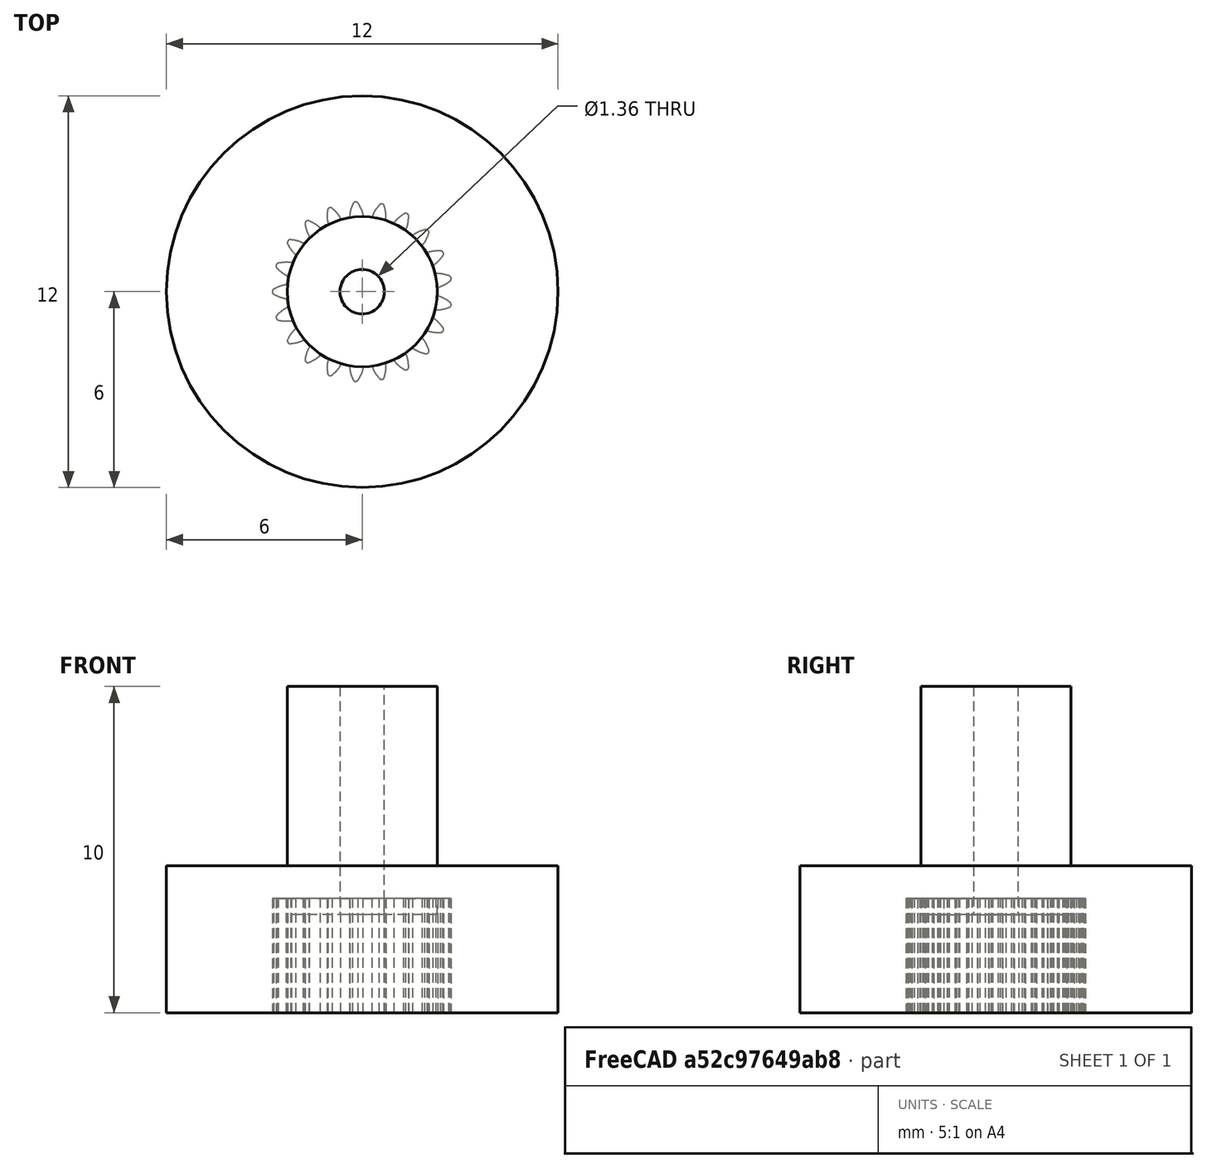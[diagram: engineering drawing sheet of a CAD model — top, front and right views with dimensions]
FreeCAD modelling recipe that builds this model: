
FCSTD DOCUMENT  (FreeCAD 0.20R29177 (Git))
Label: LC Servo top 21x024intgear short5mm
License: All rights reserved
LicenseURL: http://en.wikipedia.org/wiki/All_rights_reserved
objects: PartDesign::Body×2, PartDesign::AdditiveCylinder×2, Part::Part2DObjectPython×1, PartDesign::Pad×1, PartDesign::Boolean×1, PartDesign::SubtractiveCylinder×1, TechDraw::DrawSVGTemplate×1, PartDesign::SubtractiveBox×1, TechDraw::DrawViewPart×1, TechDraw::DrawPage×1
note: 14 computed .brp shape members not serialized (recipe doc carries the construction recipe); baked Part::Feature solids carry a one-line shape summary decoded from their .brp

FEATURE [Part::Part2DObjectPython] InvoluteGear  # Draft 2D object (typed FeaturePython)
  ExternalGear = false
  HighPrecision = true
  Modules = 0.235
  NumberOfTeeth = 21
  PressureAngle = 20
FEATURE [PartDesign::Pad] Pad
  AllowMultiFace = false
  Direction = (0,0,1)
  Length = 3.5
  Length2 = 100
  Profile = -> InvoluteGear
  Type = 0
FEATURE [PartDesign::Body] Body
  Group = -> [InvoluteGear,Pad]
  Origin = -> Origin
  Tip = -> Pad
FEATURE [PartDesign::AdditiveCylinder] Cylinder
  Angle = 360
  AttacherType = Attacher::AttachEngine3D
  FirstAngle = 0
  Height = 4.5
  MapMode = 5
  Radius = 6
  SecondAngle = 0
  Support = -> [XY_Plane001]
FEATURE [PartDesign::Boolean] Boolean
  BaseFeature = -> Cylinder
  Group = -> [Body]
  Type = 1
FEATURE [PartDesign::AdditiveCylinder] Cylinder001
  Angle = 360
  AttacherType = Attacher::AttachEngine3D
  AttachmentOffset = pos=(0,0,3) rot=(0,0,1;0rad)
  BaseFeature = -> Boolean
  FirstAngle = 0
  Height = 19
  MapMode = 5
  Placement = pos=(0,0,3) rot=(0,0,1;0rad)
  Radius = 2.3
  SecondAngle = 0
  Support = -> [XY_Plane001]
FEATURE [PartDesign::SubtractiveCylinder] Cylinder002
  Angle = 360
  AttacherType = Attacher::AttachEngine3D
  BaseFeature = -> Cylinder001
  FirstAngle = 0
  Height = 23
  MapMode = 5
  Radius = 0.68
  SecondAngle = 0
  Support = -> [XY_Plane001]
FEATURE [TechDraw::DrawSVGTemplate] Template
  EditableTexts = Designed_by_Name=Designed by Name; Drawing_number=Drawing number; FC-Date=Date; FC-SC=Scale; FC-SH=Sheet; FC-Title=Title; Subtitle=Subtitle; Weight=Weight
  Height = 210
  Orientation = 1
  Width = 297
FEATURE [PartDesign::SubtractiveBox] Box
  AttacherType = Attacher::AttachEngine3D
  AttachmentOffset = pos=(-5,-5,10) rot=(0,0,1;0rad)
  BaseFeature = -> Cylinder002
  Height = 12
  Length = 10
  MapMode = 5
  Placement = pos=(-5,-5,10) rot=(0,0,1;0rad)
  Support = -> [XY_Plane001]
  Width = 10
FEATURE [PartDesign::Body] Body001
  Group = -> [Cylinder,Boolean,Cylinder001,Cylinder002,Box]
  Origin = -> Origin001
  Tip = -> Box
FEATURE [TechDraw::DrawViewPart] View
  CoarseView = false
  Direction = (-0.021,-0.015,-1)
  Focus = 100
  HardHidden = false
  IsoCount = 0
  IsoHidden = false
  IsoVisible = false
  LockPosition = false
  Perspective = false
  Rotation = 0
  ScaleType = 0
  SeamHidden = false
  SeamVisible = false
  SmoothHidden = false
  SmoothVisible = false
  Source = -> [Body001]
  X = 148.5
  XDirection = (0.581238,-0.813733,0)
  Y = 105
FEATURE [TechDraw::DrawPage] Page
  KeepUpdated = true
  NextBalloonIndex = 1
  ProjectionType = 0
  Template = -> Template
  Views = -> [View]
